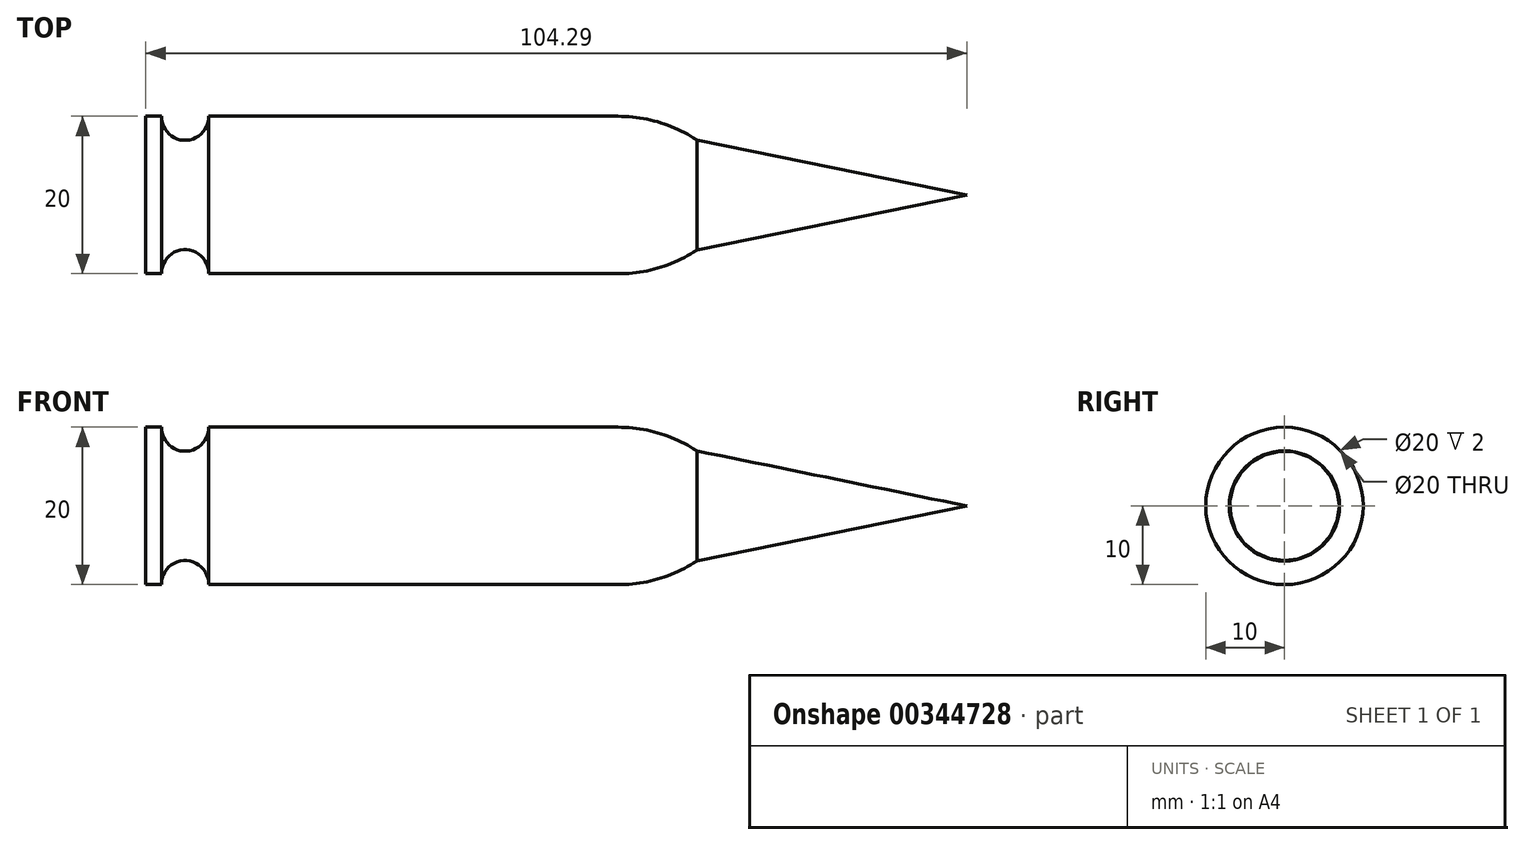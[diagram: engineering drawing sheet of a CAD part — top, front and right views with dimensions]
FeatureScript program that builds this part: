
annotation { "Feature Type Name" : "Feature", "Feature Type Description" : "" }
export const myFeature = defineFeature(function(context is Context, id is Id, definition is map)
    precondition{}
    {
        {
            var Q0;
            Q0=qCreatedBy(makeId("Front.planeOp"),FACE);
            var sketch = newSketch(context, id + "F0", { "sketchPlane" : qUnion([Q0])});
            skPoint(sketch, "E0", {"position": v(0, 10) * mm});
            skLineSegment(sketch, "E1", {"start": v(0, 10) * mm, "end": v(0, 10) * mm});
            skPoint(sketch, "E2", {"position": v(8, 10) * mm});
            skPoint(sketch, "E3", {"position": v(2, 10) * mm});
            skLineSegment(sketch, "E4", {"start": v(2, 10) * mm, "end": v(2, 10) * mm});
            skLineSegment(sketch, "E5", {"start": v(8, 10) * mm, "end": v(10, 10) * mm});
            skArc(sketch, "E6", {"start": v(2, 10) * mm, "mid": v(5, 6.95) * mm, "end": v(8, 10) * mm});
            skLineSegment(sketch, "E7", {"start": v(0, 10) * mm, "end": v(2, 10) * mm});
            skLineSegment(sketch, "E8", {"start": v(10, 10) * mm, "end": v(60, 10) * mm});
            skPoint(sketch, "E9", {"position": v(70, 7) * mm});
            skArc(sketch, "E10", {"start": v(60, 10) * mm, "mid": v(65.22, 9.23) * mm, "end": v(70, 7) * mm});
            skLineSegment(sketch, "E11", {"start": v(70, 7) * mm, "end": v(104.3, 0) * mm});
            skLineSegment(sketch, "E12", {"start": v(0, 10) * mm, "end": v(0, 0) * mm});
            skSolve(sketch);
        }
        {
            var Q0;
            Q0=qCreatedBy(makeId("Front.planeOp"),FACE);
            var sketch = newSketch(context, id + "F1", { "sketchPlane" : qUnion([Q0])});
            skLineSegment(sketch, "E13", {"start": v(-63.74, 0) * mm, "end": v(-37.96, 0) * mm});
            skSolve(sketch);
        }
        {
            var Q0;
            Q0 = qConstructionFilter(qBodyType(qCreatedBy(id + "F0" ,EDGE), BodyType.WIRE), ConstructionObject.NO);
            var Q1;
            Q1=sQuery(id+"F1.wireOp",EDGE,"E13");
            revolve(context, id + "F2", {"bodyType" : ToolBodyType.SURFACE, "surfaceEntities" : qUnion([Q0]), "axis" : qUnion([Q1]), "revolveType" : RevolveType.FULL});
        }
    });
